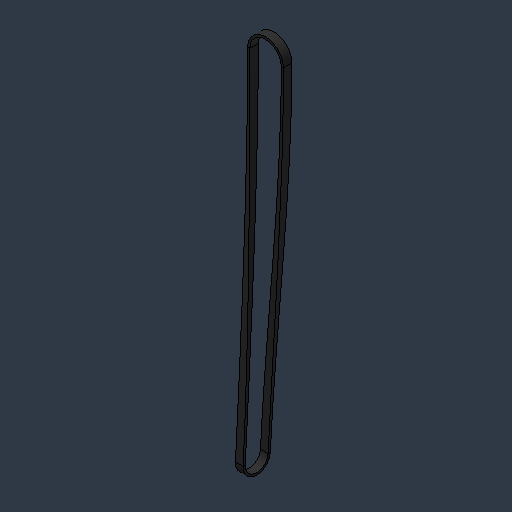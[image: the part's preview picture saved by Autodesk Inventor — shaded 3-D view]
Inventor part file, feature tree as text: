
AUTODESK INVENTOR PART (.ipt)
format: ipt  version: 2024.3 (Build 283343000, 343)  size: 196,096 bytes
history: native  units: mm (DEFAULTED — no unit token found)
features: other x4, extrude x2, loft x2, sketch x2
ambient origin geometry x8: Origin, YZ Plane, XZ Plane, XY Plane, X Axis, Y Axis, Z Axis, Center Point
bodies: Solid1 (feature_tree)
feature tree (10):
  extrude  "Extrusion1"  Depth=10.0mm TaperAngle=0.0deg
  extrude  "Extrusion2"  Depth=6.0mm TaperAngle=0.0deg
  loft  "Loft1"
  loft  "Loft2"
  sketch  "Sketch2"  dims[d0=2.5mm d1=10.0mm d2=0.0mm]
  sketch  "Sketch3"  dims[d3=2.5mm d4=6.0mm d5=3.0mm d6=0.0mm d7=0.0mm d8=10.0mm d9=90.0deg d10=10.0mm d11=90.0deg d12=10.0mm d13=90.0deg d14=10.0mm d15=90.0deg]
  other  "Edges1"
  other  "Edges2"
  other  "Edges3"
  other  "Edges4"
